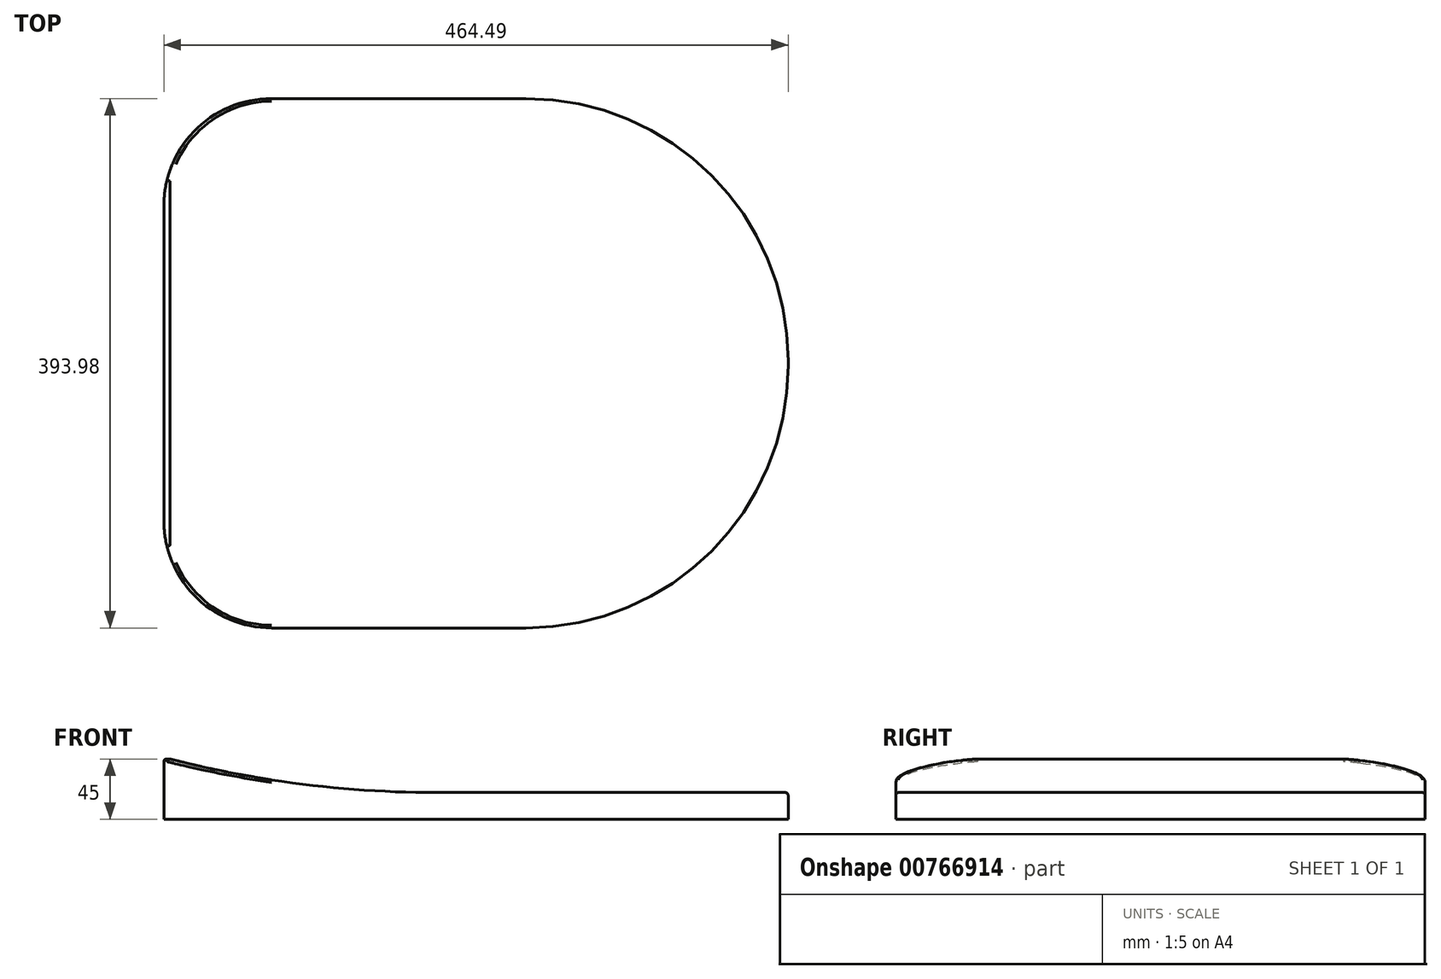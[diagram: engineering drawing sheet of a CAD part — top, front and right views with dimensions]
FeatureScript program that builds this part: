
annotation { "Feature Type Name" : "Feature", "Feature Type Description" : "" }
export const myFeature = defineFeature(function(context is Context, id is Id, definition is map)
    precondition{}
    {
        {
            var Q0;
            Q0=qCreatedBy(makeId("Top.planeOp"),FACE);
            var sketch = newSketch(context, id + "F0", { "sketchPlane" : qUnion([Q0])});
            skLineSegment(sketch, "E0.bottom", {"start": v(0, 0) * mm, "end": v(464.49, 0) * mm});
            skLineSegment(sketch, "E0.top", {"start": v(0, -393.98) * mm, "end": v(464.49, -393.98) * mm});
            skLineSegment(sketch, "E0.left", {"start": v(0, 0) * mm, "end": v(0, -393.98) * mm});
            skLineSegment(sketch, "E0.right", {"start": v(464.49, 0) * mm, "end": v(464.49, -393.98) * mm});
            skSolve(sketch);
        }
        {
            var Q0;
            Q0 = qSketchRegion(id + "F0", true);
            extrude(context, id + "F1", {"entities" : qUnion([Q0]), "depth" : 20 * mm, "offsetDistance" : 25 * mm});
        }
        {
            var Q0;
            Q0=makeQuery(id+"F1.opExtrude","CAP_FACE",FACE,{"disambiguationData":[OSD([sQuery(id+"F0.wireOp",EDGE,"E0.bottom"),sQuery(id+"F0.wireOp",EDGE,"E0.top"),sQuery(id+"F0.wireOp",EDGE,"E0.left"),sQuery(id+"F0.wireOp",EDGE,"E0.right")])],"isStart":false});
            var sketch = newSketch(context, id + "F2", { "sketchPlane" : qUnion([Q0])});
            skLineSegment(sketch, "E1.bottom", {"start": v(0, 0) * mm, "end": v(104.52, 0) * mm});
            skLineSegment(sketch, "E1.top", {"start": v(0, -393.98) * mm, "end": v(104.52, -393.98) * mm});
            skLineSegment(sketch, "E1.left", {"start": v(0, 0) * mm, "end": v(0, -393.98) * mm});
            skLineSegment(sketch, "E1.right", {"start": v(104.52, 0) * mm, "end": v(104.52, -393.98) * mm});
            skSolve(sketch);
        }
        {
            var Q0;
            Q0 = qSketchRegion(id + "F2", true);
            extrude(context, id + "F3", {"entities" : qUnion([Q0]), "operationType" : NewBodyOperationType.ADD, "depth" : 25 * mm, "offsetDistance" : 25 * mm});
        }
        {
            var Q0;
            Q0=makeQuery(id+"F3.opExtrude","CAP_EDGE",EDGE,{"disambiguationData":[OSD([sQuery(id+"F2.wireOp",EDGE,"E1.right")])],"isStart":false});
            chamfer(context, id + "F4", {"entities" : qUnion([Q0]), "chamferType" : ChamferType.TWO_OFFSETS, "width1" : 25 * mm, "oppositeDirection" : false, "width2" : 100 * mm, "tangentPropagation" : true});
        }
        {
            var Q0;
            Q0=makeQuery(id+"F1.opExtrude","SWEPT_EDGE",EDGE,{"disambiguationData":[OSD([sQuery(id+"F0.wireOp",EDGE,"E0.top"),sQuery(id+"F0.wireOp",EDGE,"E0.right")])]});
            var Q1;
            Q1=makeQuery(id+"F1.opExtrude","SWEPT_EDGE",EDGE,{"disambiguationData":[OSD([sQuery(id+"F0.wireOp",EDGE,"E0.bottom"),sQuery(id+"F0.wireOp",EDGE,"E0.right")])]});
            fillet(context, id + "F5", {"entities" : qUnion([Q0, Q1]), "radius" : 195 * mm, "tangentPropagation" : true, "allowEdgeOverflow" : false});
        }
        {
            var Q0;
            Q0=makeQuery(id+"F4.opChamfer","BLEND_EDGE",EDGE,{"blendedFrom":[makeQuery(id+"F3.opExtrude","CAP_EDGE",EDGE,{"disambiguationData":[OSD([sQuery(id+"F2.wireOp",EDGE,"E1.right")])],"isStart":false}),makeQuery(id+"F1.opExtrude","CAP_FACE",FACE,{"disambiguationData":[OSD([sQuery(id+"F0.wireOp",EDGE,"E0.bottom"),sQuery(id+"F0.wireOp",EDGE,"E0.top"),sQuery(id+"F0.wireOp",EDGE,"E0.left"),sQuery(id+"F0.wireOp",EDGE,"E0.right")])],"isStart":false})],"blendedInto":[makeQuery(id+"F1.opExtrude","CAP_FACE",FACE,{"disambiguationData":[OSD([sQuery(id+"F0.wireOp",EDGE,"E0.bottom"),sQuery(id+"F0.wireOp",EDGE,"E0.top"),sQuery(id+"F0.wireOp",EDGE,"E0.left"),sQuery(id+"F0.wireOp",EDGE,"E0.right")])],"isStart":false})]});
            fillet(context, id + "F6", {"entities" : qUnion([Q0]), "radius" : 800 * mm, "tangentPropagation" : true, "allowEdgeOverflow" : false});
        }
        {
            var Q0;
            Q0=makeQuery(id+"F3.boolean.opBoolean","MERGE",EDGE,{"derivedFrom":[makeQuery(id+"F1.opExtrude","SWEPT_EDGE",EDGE,{"disambiguationData":[OSD([sQuery(id+"F0.wireOp",EDGE,"E0.top"),sQuery(id+"F0.wireOp",EDGE,"E0.left")])]}),makeQuery(id+"F3.opExtrude","SWEPT_EDGE",EDGE,{"disambiguationData":[OSD([sQuery(id+"F2.wireOp",EDGE,"E1.top"),sQuery(id+"F2.wireOp",EDGE,"E1.left")])]})]});
            var Q1;
            Q1=makeQuery(id+"F3.boolean.opBoolean","MERGE",EDGE,{"derivedFrom":[makeQuery(id+"F1.opExtrude","SWEPT_EDGE",EDGE,{"disambiguationData":[OSD([sQuery(id+"F0.wireOp",EDGE,"E0.bottom"),sQuery(id+"F0.wireOp",EDGE,"E0.left")])]}),makeQuery(id+"F3.opExtrude","SWEPT_EDGE",EDGE,{"disambiguationData":[OSD([sQuery(id+"F2.wireOp",EDGE,"E1.bottom"),sQuery(id+"F2.wireOp",EDGE,"E1.left")])]})]});
            fillet(context, id + "F7", {"entities" : qUnion([Q0, Q1]), "radius" : 80 * mm, "tangentPropagation" : true, "allowEdgeOverflow" : false});
        }
        {
            var Q0;
            {var subQ0=sQuery(id+"F0.wireOp",EDGE,"E0.left");var subQ1=sQuery(id+"F0.wireOp",EDGE,"E0.top");Q0=makeQuery(id+"F7.opFillet","BLEND_EDGE",EDGE,{"blendedFrom":[makeQuery(id+"F3.boolean.opBoolean","MERGE",EDGE,{"derivedFrom":[makeQuery(id+"F1.opExtrude","SWEPT_EDGE",EDGE,{"disambiguationData":[OSD([subQ1,subQ0])]}),makeQuery(id+"F3.opExtrude","SWEPT_EDGE",EDGE,{"disambiguationData":[OSD([sQuery(id+"F2.wireOp",EDGE,"E1.top"),sQuery(id+"F2.wireOp",EDGE,"E1.left")])]})]}),makeQuery(id+"F6.opFillet","BLEND_FACE",FACE,{"disambiguationData":[OSD([sQuery(id+"F0.wireOp",EDGE,"E0.bottom"),subQ1,subQ0,sQuery(id+"F0.wireOp",EDGE,"E0.right"),sQuery(id+"F2.wireOp",EDGE,"E1.right")])]})],"blendedInto":[makeQuery(id+"F6.opFillet","BLEND_FACE",FACE,{"disambiguationData":[OSD([sQuery(id+"F0.wireOp",EDGE,"E0.bottom"),subQ1,subQ0,sQuery(id+"F0.wireOp",EDGE,"E0.right"),sQuery(id+"F2.wireOp",EDGE,"E1.right")])]})]});}
            var Q1;
            {var subQ0=sQuery(id+"F0.wireOp",EDGE,"E0.top");Q1=makeQuery(id+"F6.opFillet","BLEND_EDGE",EDGE,{"blendedFrom":[makeQuery(id+"F4.opChamfer","BLEND_EDGE",EDGE,{"blendedFrom":[makeQuery(id+"F3.opExtrude","CAP_EDGE",EDGE,{"disambiguationData":[OSD([sQuery(id+"F2.wireOp",EDGE,"E1.right")])],"isStart":false}),makeQuery(id+"F1.opExtrude","CAP_FACE",FACE,{"disambiguationData":[OSD([sQuery(id+"F0.wireOp",EDGE,"E0.bottom"),subQ0,sQuery(id+"F0.wireOp",EDGE,"E0.left"),sQuery(id+"F0.wireOp",EDGE,"E0.right")])],"isStart":false})],"blendedInto":[makeQuery(id+"F1.opExtrude","CAP_FACE",FACE,{"disambiguationData":[OSD([sQuery(id+"F0.wireOp",EDGE,"E0.bottom"),subQ0,sQuery(id+"F0.wireOp",EDGE,"E0.left"),sQuery(id+"F0.wireOp",EDGE,"E0.right")])],"isStart":false})]}),makeQuery(id+"F3.boolean.opBoolean","MERGE",FACE,{"derivedFrom":[makeQuery(id+"F1.opExtrude","SWEPT_FACE",FACE,{"disambiguationData":[OSD([subQ0])]}),makeQuery(id+"F3.opExtrude","SWEPT_FACE",FACE,{"disambiguationData":[OSD([sQuery(id+"F2.wireOp",EDGE,"E1.top")])]})]})],"blendedInto":[makeQuery(id+"F3.boolean.opBoolean","MERGE",FACE,{"derivedFrom":[makeQuery(id+"F1.opExtrude","SWEPT_FACE",FACE,{"disambiguationData":[OSD([subQ0])]}),makeQuery(id+"F3.opExtrude","SWEPT_FACE",FACE,{"disambiguationData":[OSD([sQuery(id+"F2.wireOp",EDGE,"E1.top")])]})]})]});}
            var Q2;
            Q2=makeQuery(id+"F1.opExtrude","CAP_EDGE",EDGE,{"disambiguationData":[OSD([sQuery(id+"F0.wireOp",EDGE,"E0.top")])],"isStart":false});
            var Q3;
            {var subQ0=sQuery(id+"F0.wireOp",EDGE,"E0.right");var subQ1=sQuery(id+"F0.wireOp",EDGE,"E0.top");Q3=makeQuery(id+"F5.opFillet","BLEND_EDGE",EDGE,{"blendedFrom":[makeQuery(id+"F1.opExtrude","SWEPT_EDGE",EDGE,{"disambiguationData":[OSD([subQ1,subQ0])]}),makeQuery(id+"F1.opExtrude","CAP_FACE",FACE,{"disambiguationData":[OSD([sQuery(id+"F0.wireOp",EDGE,"E0.bottom"),subQ1,sQuery(id+"F0.wireOp",EDGE,"E0.left"),subQ0])],"isStart":false})],"blendedInto":[makeQuery(id+"F1.opExtrude","CAP_FACE",FACE,{"disambiguationData":[OSD([sQuery(id+"F0.wireOp",EDGE,"E0.bottom"),subQ1,sQuery(id+"F0.wireOp",EDGE,"E0.left"),subQ0])],"isStart":false})]});}
            var Q4;
            Q4=makeQuery(id+"F1.opExtrude","CAP_EDGE",EDGE,{"disambiguationData":[OSD([sQuery(id+"F0.wireOp",EDGE,"E0.right")])],"isStart":false});
            var Q5;
            {var subQ0=sQuery(id+"F0.wireOp",EDGE,"E0.right");var subQ1=sQuery(id+"F0.wireOp",EDGE,"E0.bottom");Q5=makeQuery(id+"F5.opFillet","BLEND_EDGE",EDGE,{"blendedFrom":[makeQuery(id+"F1.opExtrude","SWEPT_EDGE",EDGE,{"disambiguationData":[OSD([subQ1,subQ0])]}),makeQuery(id+"F1.opExtrude","CAP_FACE",FACE,{"disambiguationData":[OSD([subQ1,sQuery(id+"F0.wireOp",EDGE,"E0.top"),sQuery(id+"F0.wireOp",EDGE,"E0.left"),subQ0])],"isStart":false})],"blendedInto":[makeQuery(id+"F1.opExtrude","CAP_FACE",FACE,{"disambiguationData":[OSD([subQ1,sQuery(id+"F0.wireOp",EDGE,"E0.top"),sQuery(id+"F0.wireOp",EDGE,"E0.left"),subQ0])],"isStart":false})]});}
            var Q6;
            Q6=makeQuery(id+"F1.opExtrude","CAP_EDGE",EDGE,{"disambiguationData":[OSD([sQuery(id+"F0.wireOp",EDGE,"E0.bottom")])],"isStart":false});
            var Q7;
            {var subQ0=sQuery(id+"F0.wireOp",EDGE,"E0.bottom");Q7=makeQuery(id+"F6.opFillet","BLEND_EDGE",EDGE,{"blendedFrom":[makeQuery(id+"F4.opChamfer","BLEND_EDGE",EDGE,{"blendedFrom":[makeQuery(id+"F3.opExtrude","CAP_EDGE",EDGE,{"disambiguationData":[OSD([sQuery(id+"F2.wireOp",EDGE,"E1.right")])],"isStart":false}),makeQuery(id+"F1.opExtrude","CAP_FACE",FACE,{"disambiguationData":[OSD([subQ0,sQuery(id+"F0.wireOp",EDGE,"E0.top"),sQuery(id+"F0.wireOp",EDGE,"E0.left"),sQuery(id+"F0.wireOp",EDGE,"E0.right")])],"isStart":false})],"blendedInto":[makeQuery(id+"F1.opExtrude","CAP_FACE",FACE,{"disambiguationData":[OSD([subQ0,sQuery(id+"F0.wireOp",EDGE,"E0.top"),sQuery(id+"F0.wireOp",EDGE,"E0.left"),sQuery(id+"F0.wireOp",EDGE,"E0.right")])],"isStart":false})]}),makeQuery(id+"F3.boolean.opBoolean","MERGE",FACE,{"derivedFrom":[makeQuery(id+"F1.opExtrude","SWEPT_FACE",FACE,{"disambiguationData":[OSD([subQ0])]}),makeQuery(id+"F3.opExtrude","SWEPT_FACE",FACE,{"disambiguationData":[OSD([sQuery(id+"F2.wireOp",EDGE,"E1.bottom")])]})]})],"blendedInto":[makeQuery(id+"F3.boolean.opBoolean","MERGE",FACE,{"derivedFrom":[makeQuery(id+"F1.opExtrude","SWEPT_FACE",FACE,{"disambiguationData":[OSD([subQ0])]}),makeQuery(id+"F3.opExtrude","SWEPT_FACE",FACE,{"disambiguationData":[OSD([sQuery(id+"F2.wireOp",EDGE,"E1.bottom")])]})]})]});}
            var Q8;
            {var subQ0=sQuery(id+"F0.wireOp",EDGE,"E0.left");var subQ1=sQuery(id+"F0.wireOp",EDGE,"E0.bottom");Q8=makeQuery(id+"F7.opFillet","BLEND_EDGE",EDGE,{"blendedFrom":[makeQuery(id+"F3.boolean.opBoolean","MERGE",EDGE,{"derivedFrom":[makeQuery(id+"F1.opExtrude","SWEPT_EDGE",EDGE,{"disambiguationData":[OSD([subQ1,subQ0])]}),makeQuery(id+"F3.opExtrude","SWEPT_EDGE",EDGE,{"disambiguationData":[OSD([sQuery(id+"F2.wireOp",EDGE,"E1.bottom"),sQuery(id+"F2.wireOp",EDGE,"E1.left")])]})]}),makeQuery(id+"F6.opFillet","BLEND_FACE",FACE,{"disambiguationData":[OSD([subQ1,sQuery(id+"F0.wireOp",EDGE,"E0.top"),subQ0,sQuery(id+"F0.wireOp",EDGE,"E0.right"),sQuery(id+"F2.wireOp",EDGE,"E1.right")])]})],"blendedInto":[makeQuery(id+"F6.opFillet","BLEND_FACE",FACE,{"disambiguationData":[OSD([subQ1,sQuery(id+"F0.wireOp",EDGE,"E0.top"),subQ0,sQuery(id+"F0.wireOp",EDGE,"E0.right"),sQuery(id+"F2.wireOp",EDGE,"E1.right")])]})]});}
            var Q9;
            Q9=makeQuery(id+"F7.opFillet","BLEND_EDGE",EDGE,{"blendedFrom":[makeQuery(id+"F3.boolean.opBoolean","MERGE",EDGE,{"derivedFrom":[makeQuery(id+"F1.opExtrude","SWEPT_EDGE",EDGE,{"disambiguationData":[OSD([sQuery(id+"F0.wireOp",EDGE,"E0.bottom"),sQuery(id+"F0.wireOp",EDGE,"E0.left")])]}),makeQuery(id+"F3.opExtrude","SWEPT_EDGE",EDGE,{"disambiguationData":[OSD([sQuery(id+"F2.wireOp",EDGE,"E1.bottom"),sQuery(id+"F2.wireOp",EDGE,"E1.left")])]})]}),makeQuery(id+"F4.opChamfer","BLEND_FACE",FACE,{"disambiguationData":[OSD([sQuery(id+"F2.wireOp",EDGE,"E1.right")])]})],"blendedInto":[makeQuery(id+"F4.opChamfer","BLEND_FACE",FACE,{"disambiguationData":[OSD([sQuery(id+"F2.wireOp",EDGE,"E1.right")])]})]});
            var Q10;
            {var subQ0=sQuery(id+"F2.wireOp",EDGE,"E1.left");var subQ1=sQuery(id+"F2.wireOp",EDGE,"E1.top");Q10=makeQuery(id+"F7.opFillet","BLEND_EDGE",EDGE,{"blendedFrom":[makeQuery(id+"F3.boolean.opBoolean","MERGE",EDGE,{"derivedFrom":[makeQuery(id+"F1.opExtrude","SWEPT_EDGE",EDGE,{"disambiguationData":[OSD([sQuery(id+"F0.wireOp",EDGE,"E0.top"),sQuery(id+"F0.wireOp",EDGE,"E0.left")])]}),makeQuery(id+"F3.opExtrude","SWEPT_EDGE",EDGE,{"disambiguationData":[OSD([subQ1,subQ0])]})]}),makeQuery(id+"F3.opExtrude","CAP_FACE",FACE,{"disambiguationData":[OSD([sQuery(id+"F2.wireOp",EDGE,"E1.bottom"),subQ1,subQ0,sQuery(id+"F2.wireOp",EDGE,"E1.right")])],"isStart":false})],"blendedInto":[makeQuery(id+"F3.opExtrude","CAP_FACE",FACE,{"disambiguationData":[OSD([sQuery(id+"F2.wireOp",EDGE,"E1.bottom"),subQ1,subQ0,sQuery(id+"F2.wireOp",EDGE,"E1.right")])],"isStart":false})]});}
            fillet(context, id + "F8", {"entities" : qUnion([Q0, Q1, Q2, Q3, Q4, Q5, Q6, Q7, Q8, Q9, Q10]), "radius" : 2 * mm, "tangentPropagation" : true, "allowEdgeOverflow" : false});
        }
    });
